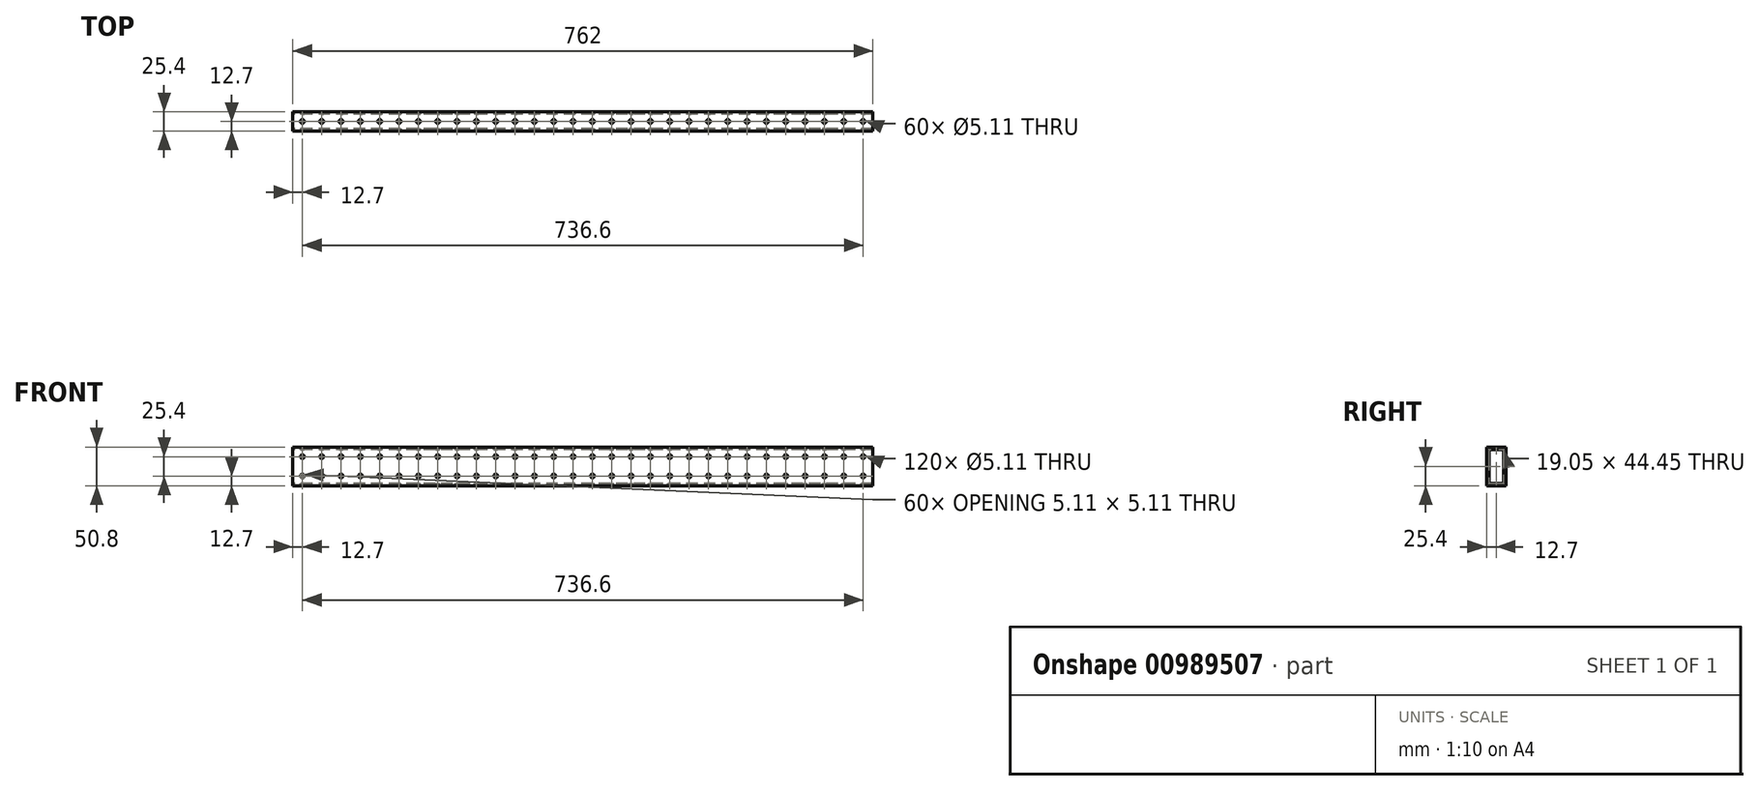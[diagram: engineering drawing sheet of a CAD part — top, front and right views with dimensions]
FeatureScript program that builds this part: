
annotation { "Feature Type Name" : "Feature", "Feature Type Description" : "" }
export const myFeature = defineFeature(function(context is Context, id is Id, definition is map)
    precondition{}
    {
        {
            var Q0;
            Q0=qCreatedBy(makeId("Right.planeOp"),FACE);
            var sketch = newSketch(context, id + "F0", { "sketchPlane" : qUnion([Q0])});
            skLineSegment(sketch, "E0.bottom", {"start": v(12.7, 25.4) * mm, "end": v(-12.7, 25.4) * mm});
            skLineSegment(sketch, "E0.top", {"start": v(12.7, -25.4) * mm, "end": v(-12.7, -25.4) * mm});
            skLineSegment(sketch, "E0.left", {"start": v(12.7, 25.4) * mm, "end": v(12.7, -25.4) * mm});
            skLineSegment(sketch, "E0.right", {"start": v(-12.7, 25.4) * mm, "end": v(-12.7, -25.4) * mm});
            skPoint(sketch, "E0.middle", {"position": v(0, 0) * mm});
            skLineSegment(sketch, "E1.0", {"start": v(9.52, 22.22) * mm, "end": v(-9.53, 22.22) * mm});
            skLineSegment(sketch, "E1.1", {"start": v(9.52, 22.22) * mm, "end": v(9.53, -22.23) * mm});
            skLineSegment(sketch, "E1.2", {"start": v(9.53, -22.23) * mm, "end": v(-9.52, -22.23) * mm});
            skLineSegment(sketch, "E1.3", {"start": v(-9.53, 22.22) * mm, "end": v(-9.52, -22.23) * mm});
            skSolve(sketch);
        }
        {
            var Q0;
            Q0 = qSketchRegion(id + "F0", true);
            extrude(context, id + "F1", {"entities" : qUnion([Q0]), "depth" : 762 * mm, "offsetDistance" : 25.4 * mm});
        }
        {
            var Q0;
            Q0=makeQuery(id+"F1.opExtrude","SWEPT_FACE",FACE,{"disambiguationData":[OSD([sQuery(id+"F0.wireOp",EDGE,"E0.bottom")])]});
            var sketch = newSketch(context, id + "F2", { "sketchPlane" : qUnion([Q0])});
            skCircle(sketch, "E2", {"center": v(12.7, 0) * mm, "radius": 2.55 * mm});
            skCircle(sketch, "E3.1.0.0", {"center": v(38.1, 0) * mm, "radius": 2.55 * mm});
            skCircle(sketch, "E3.2.0.0", {"center": v(63.5, 0) * mm, "radius": 2.55 * mm});
            skCircle(sketch, "E3.3.0.0", {"center": v(88.9, 0) * mm, "radius": 2.55 * mm});
            skCircle(sketch, "E3.4.0.0", {"center": v(114.3, 0) * mm, "radius": 2.55 * mm});
            skCircle(sketch, "E3.5.0.0", {"center": v(139.7, 0) * mm, "radius": 2.55 * mm});
            skCircle(sketch, "E3.6.0.0", {"center": v(165.1, 0) * mm, "radius": 2.55 * mm});
            skCircle(sketch, "E3.7.0.0", {"center": v(190.5, 0) * mm, "radius": 2.55 * mm});
            skCircle(sketch, "E3.8.0.0", {"center": v(215.9, 0) * mm, "radius": 2.55 * mm});
            skCircle(sketch, "E3.9.0.0", {"center": v(241.3, 0) * mm, "radius": 2.55 * mm});
            skCircle(sketch, "E3.10.0.0", {"center": v(266.7, 0) * mm, "radius": 2.55 * mm});
            skCircle(sketch, "E3.11.0.0", {"center": v(292.1, 0) * mm, "radius": 2.55 * mm});
            skCircle(sketch, "E3.12.0.0", {"center": v(317.5, 0) * mm, "radius": 2.55 * mm});
            skCircle(sketch, "E3.13.0.0", {"center": v(342.9, 0) * mm, "radius": 2.55 * mm});
            skCircle(sketch, "E3.14.0.0", {"center": v(368.3, 0) * mm, "radius": 2.55 * mm});
            skCircle(sketch, "E3.15.0.0", {"center": v(393.7, 0) * mm, "radius": 2.55 * mm});
            skCircle(sketch, "E3.16.0.0", {"center": v(419.1, 0) * mm, "radius": 2.55 * mm});
            skCircle(sketch, "E3.17.0.0", {"center": v(444.5, 0) * mm, "radius": 2.55 * mm});
            skCircle(sketch, "E3.18.0.0", {"center": v(469.9, 0) * mm, "radius": 2.55 * mm});
            skCircle(sketch, "E3.19.0.0", {"center": v(495.3, 0) * mm, "radius": 2.55 * mm});
            skCircle(sketch, "E3.20.0.0", {"center": v(520.7, 0) * mm, "radius": 2.55 * mm});
            skCircle(sketch, "E3.21.0.0", {"center": v(546.1, 0) * mm, "radius": 2.55 * mm});
            skCircle(sketch, "E3.22.0.0", {"center": v(571.5, 0) * mm, "radius": 2.55 * mm});
            skCircle(sketch, "E3.23.0.0", {"center": v(596.9, 0) * mm, "radius": 2.55 * mm});
            skCircle(sketch, "E3.24.0.0", {"center": v(622.3, 0) * mm, "radius": 2.55 * mm});
            skCircle(sketch, "E3.25.0.0", {"center": v(647.7, 0) * mm, "radius": 2.55 * mm});
            skCircle(sketch, "E3.26.0.0", {"center": v(673.1, 0) * mm, "radius": 2.55 * mm});
            skCircle(sketch, "E3.27.0.0", {"center": v(698.5, 0) * mm, "radius": 2.55 * mm});
            skCircle(sketch, "E3.28.0.0", {"center": v(723.9, 0) * mm, "radius": 2.55 * mm});
            skCircle(sketch, "E3.29.0.0", {"center": v(749.3, 0) * mm, "radius": 2.55 * mm});
            skLineSegment(sketch, "E3.direction1", {"start": v(12.7, 0) * mm, "end": v(38.1, 0) * mm, "construction": true});
            skSolve(sketch);
        }
        {
            var Q0;
            Q0 = qSketchRegion(id + "F2", true);
            extrude(context, id + "F3", {"entities" : qUnion([Q0]), "operationType" : NewBodyOperationType.REMOVE, "endBound" : BoundingType.THROUGH_ALL, "oppositeDirection" : true, "depth" : 25.4 * mm, "offsetDistance" : 25.4 * mm});
        }
        {
            var Q0;
            Q0=makeQuery(id+"F1.opExtrude","SWEPT_FACE",FACE,{"disambiguationData":[OSD([sQuery(id+"F0.wireOp",EDGE,"E0.right")])]});
            var sketch = newSketch(context, id + "F4", { "sketchPlane" : qUnion([Q0])});
            skCircle(sketch, "E4", {"center": v(12.7, 12.7) * mm, "radius": 2.55 * mm});
            skCircle(sketch, "E5.0.1.0", {"center": v(12.7, -12.7) * mm, "radius": 2.55 * mm});
            skCircle(sketch, "E5.1.0.0", {"center": v(38.1, 12.7) * mm, "radius": 2.55 * mm});
            skCircle(sketch, "E5.1.1.0", {"center": v(38.1, -12.7) * mm, "radius": 2.55 * mm});
            skCircle(sketch, "E5.2.0.0", {"center": v(63.5, 12.7) * mm, "radius": 2.55 * mm});
            skCircle(sketch, "E5.2.1.0", {"center": v(63.5, -12.7) * mm, "radius": 2.55 * mm});
            skCircle(sketch, "E5.3.0.0", {"center": v(88.9, 12.7) * mm, "radius": 2.55 * mm});
            skCircle(sketch, "E5.3.1.0", {"center": v(88.9, -12.7) * mm, "radius": 2.55 * mm});
            skCircle(sketch, "E5.4.0.0", {"center": v(114.3, 12.7) * mm, "radius": 2.55 * mm});
            skCircle(sketch, "E5.4.1.0", {"center": v(114.3, -12.7) * mm, "radius": 2.55 * mm});
            skCircle(sketch, "E5.5.0.0", {"center": v(139.7, 12.7) * mm, "radius": 2.55 * mm});
            skCircle(sketch, "E5.5.1.0", {"center": v(139.7, -12.7) * mm, "radius": 2.55 * mm});
            skCircle(sketch, "E5.6.0.0", {"center": v(165.1, 12.7) * mm, "radius": 2.55 * mm});
            skCircle(sketch, "E5.6.1.0", {"center": v(165.1, -12.7) * mm, "radius": 2.55 * mm});
            skCircle(sketch, "E5.7.0.0", {"center": v(190.5, 12.7) * mm, "radius": 2.55 * mm});
            skCircle(sketch, "E5.7.1.0", {"center": v(190.5, -12.7) * mm, "radius": 2.55 * mm});
            skCircle(sketch, "E5.8.0.0", {"center": v(215.9, 12.7) * mm, "radius": 2.55 * mm});
            skCircle(sketch, "E5.8.1.0", {"center": v(215.9, -12.7) * mm, "radius": 2.55 * mm});
            skCircle(sketch, "E5.9.0.0", {"center": v(241.3, 12.7) * mm, "radius": 2.55 * mm});
            skCircle(sketch, "E5.9.1.0", {"center": v(241.3, -12.7) * mm, "radius": 2.55 * mm});
            skCircle(sketch, "E5.10.0.0", {"center": v(266.7, 12.7) * mm, "radius": 2.55 * mm});
            skCircle(sketch, "E5.10.1.0", {"center": v(266.7, -12.7) * mm, "radius": 2.55 * mm});
            skCircle(sketch, "E5.11.0.0", {"center": v(292.1, 12.7) * mm, "radius": 2.55 * mm});
            skCircle(sketch, "E5.11.1.0", {"center": v(292.1, -12.7) * mm, "radius": 2.55 * mm});
            skCircle(sketch, "E5.12.0.0", {"center": v(317.5, 12.7) * mm, "radius": 2.55 * mm});
            skCircle(sketch, "E5.12.1.0", {"center": v(317.5, -12.7) * mm, "radius": 2.55 * mm});
            skCircle(sketch, "E5.13.0.0", {"center": v(342.9, 12.7) * mm, "radius": 2.55 * mm});
            skCircle(sketch, "E5.13.1.0", {"center": v(342.9, -12.7) * mm, "radius": 2.55 * mm});
            skCircle(sketch, "E5.14.0.0", {"center": v(368.3, 12.7) * mm, "radius": 2.55 * mm});
            skCircle(sketch, "E5.14.1.0", {"center": v(368.3, -12.7) * mm, "radius": 2.55 * mm});
            skCircle(sketch, "E5.15.0.0", {"center": v(393.7, 12.7) * mm, "radius": 2.55 * mm});
            skCircle(sketch, "E5.15.1.0", {"center": v(393.7, -12.7) * mm, "radius": 2.55 * mm});
            skCircle(sketch, "E5.16.0.0", {"center": v(419.1, 12.7) * mm, "radius": 2.55 * mm});
            skCircle(sketch, "E5.16.1.0", {"center": v(419.1, -12.7) * mm, "radius": 2.55 * mm});
            skCircle(sketch, "E5.17.0.0", {"center": v(444.5, 12.7) * mm, "radius": 2.55 * mm});
            skCircle(sketch, "E5.17.1.0", {"center": v(444.5, -12.7) * mm, "radius": 2.55 * mm});
            skCircle(sketch, "E5.18.0.0", {"center": v(469.9, 12.7) * mm, "radius": 2.55 * mm});
            skCircle(sketch, "E5.18.1.0", {"center": v(469.9, -12.7) * mm, "radius": 2.55 * mm});
            skCircle(sketch, "E5.19.0.0", {"center": v(495.3, 12.7) * mm, "radius": 2.55 * mm});
            skCircle(sketch, "E5.19.1.0", {"center": v(495.3, -12.7) * mm, "radius": 2.55 * mm});
            skCircle(sketch, "E5.20.0.0", {"center": v(520.7, 12.7) * mm, "radius": 2.55 * mm});
            skCircle(sketch, "E5.20.1.0", {"center": v(520.7, -12.7) * mm, "radius": 2.55 * mm});
            skCircle(sketch, "E5.21.0.0", {"center": v(546.1, 12.7) * mm, "radius": 2.55 * mm});
            skCircle(sketch, "E5.21.1.0", {"center": v(546.1, -12.7) * mm, "radius": 2.55 * mm});
            skCircle(sketch, "E5.22.0.0", {"center": v(571.5, 12.7) * mm, "radius": 2.55 * mm});
            skCircle(sketch, "E5.22.1.0", {"center": v(571.5, -12.7) * mm, "radius": 2.55 * mm});
            skCircle(sketch, "E5.23.0.0", {"center": v(596.9, 12.7) * mm, "radius": 2.55 * mm});
            skCircle(sketch, "E5.23.1.0", {"center": v(596.9, -12.7) * mm, "radius": 2.55 * mm});
            skCircle(sketch, "E5.24.0.0", {"center": v(622.3, 12.7) * mm, "radius": 2.55 * mm});
            skCircle(sketch, "E5.24.1.0", {"center": v(622.3, -12.7) * mm, "radius": 2.55 * mm});
            skCircle(sketch, "E5.25.0.0", {"center": v(647.7, 12.7) * mm, "radius": 2.55 * mm});
            skCircle(sketch, "E5.25.1.0", {"center": v(647.7, -12.7) * mm, "radius": 2.55 * mm});
            skCircle(sketch, "E5.26.0.0", {"center": v(673.1, 12.7) * mm, "radius": 2.55 * mm});
            skCircle(sketch, "E5.26.1.0", {"center": v(673.1, -12.7) * mm, "radius": 2.55 * mm});
            skCircle(sketch, "E5.27.0.0", {"center": v(698.5, 12.7) * mm, "radius": 2.55 * mm});
            skCircle(sketch, "E5.27.1.0", {"center": v(698.5, -12.7) * mm, "radius": 2.55 * mm});
            skCircle(sketch, "E5.28.0.0", {"center": v(723.9, 12.7) * mm, "radius": 2.55 * mm});
            skCircle(sketch, "E5.28.1.0", {"center": v(723.9, -12.7) * mm, "radius": 2.55 * mm});
            skCircle(sketch, "E5.29.0.0", {"center": v(749.3, 12.7) * mm, "radius": 2.55 * mm});
            skCircle(sketch, "E5.29.1.0", {"center": v(749.3, -12.7) * mm, "radius": 2.55 * mm});
            skLineSegment(sketch, "E5.direction1", {"start": v(12.7, 12.7) * mm, "end": v(38.1, 12.7) * mm, "construction": true});
            skLineSegment(sketch, "E5.direction2", {"start": v(12.7, 12.7) * mm, "end": v(12.7, -12.7) * mm, "construction": true});
            skSolve(sketch);
        }
        {
            var Q0;
            Q0 = qSketchRegion(id + "F4", true);
            extrude(context, id + "F5", {"entities" : qUnion([Q0]), "operationType" : NewBodyOperationType.REMOVE, "oppositeDirection" : true, "depth" : 25.4 * mm, "offsetDistance" : 25.4 * mm});
        }
    });
